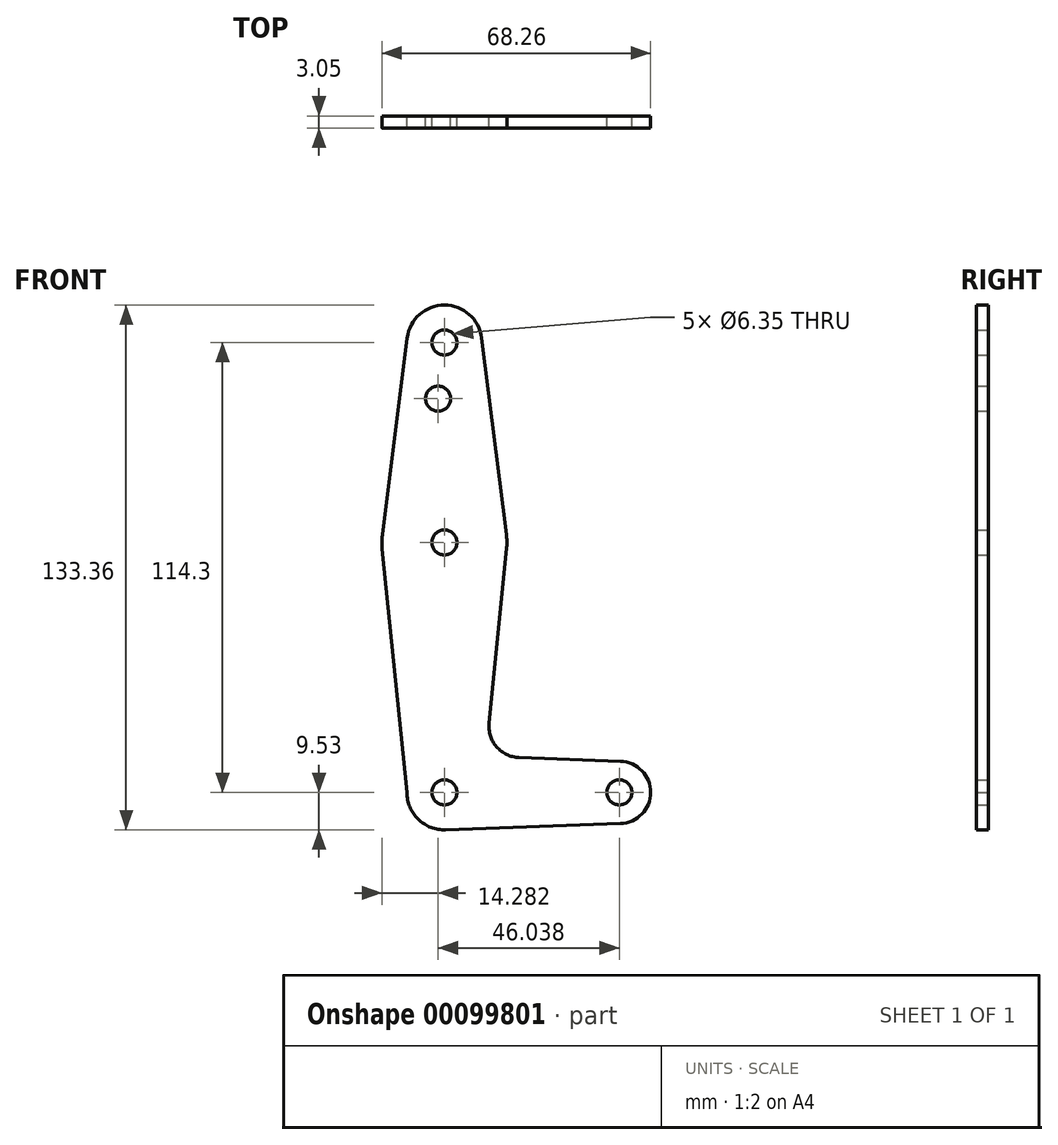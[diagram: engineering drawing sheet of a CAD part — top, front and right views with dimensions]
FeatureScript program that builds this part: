
annotation { "Feature Type Name" : "Feature", "Feature Type Description" : "" }
export const myFeature = defineFeature(function(context is Context, id is Id, definition is map)
    precondition{}
    {
        {
            var Q0;
            Q0=qCreatedBy(makeId("Front.planeOp"),FACE);
            var sketch = newSketch(context, id + "F0", { "sketchPlane" : qUnion([Q0])});
            skLineSegment(sketch, "E0", {"start": v(0, 0) * mm, "end": v(0, 114.3) * mm, "construction": true});
            skCircle(sketch, "E1", {"center": v(0, 114.3) * mm, "radius": 9.53 * mm});
            skLineSegment(sketch, "E2", {"start": v(0, 0) * mm, "end": v(44.45, 0) * mm, "construction": true});
            skCircle(sketch, "E3", {"center": v(44.45, 0) * mm, "radius": 7.94 * mm});
            skCircle(sketch, "E4", {"center": v(0, 0) * mm, "radius": 9.53 * mm});
            skCircle(sketch, "E5", {"center": v(-1.59, 100.03) * mm, "radius": 3.18 * mm});
            skCircle(sketch, "E6", {"center": v(0, 114.3) * mm, "radius": 3.18 * mm});
            skCircle(sketch, "E7", {"center": v(0, 63.5) * mm, "radius": 3.18 * mm});
            skCircle(sketch, "E8", {"center": v(44.45, 0) * mm, "radius": 3.18 * mm});
            skCircle(sketch, "E9", {"center": v(0, 0) * mm, "radius": 3.18 * mm});
            skLineSegment(sketch, "E10", {"start": v(44.73, -7.93) * mm, "end": v(0, -9.53) * mm});
            skLineSegment(sketch, "E11", {"start": v(44.73, 7.93) * mm, "end": v(18.97, 8.85) * mm});
            skCircle(sketch, "E12", {"center": v(0, 63.5) * mm, "radius": 15.88 * mm});
            skLineSegment(sketch, "E13", {"start": v(-9.45, 115.5) * mm, "end": v(-15.75, 65.48) * mm});
            skLineSegment(sketch, "E14", {"start": v(9.45, 115.5) * mm, "end": v(15.75, 65.48) * mm});
            skLineSegment(sketch, "E15", {"start": v(15.8, 61.91) * mm, "end": v(11.34, 17.6) * mm});
            skLineSegment(sketch, "E16", {"start": v(-9.52, 0) * mm, "end": v(-15.8, 61.9) * mm});
            skPoint(sketch, "E17.newPointB", {"position": v(0, 9.53) * mm});
            skArc(sketch, "E17.filletArc", {"start": v(11.34, 17.6) * mm, "mid": v(13.26, 11.57) * mm, "end": v(18.97, 8.85) * mm});
            skSolve(sketch);
        }
        {
            var Q0;
            Q0 = qSketchRegion(id + "F0", true);
            extrude(context, id + "F1", {"entities" : qUnion([Q0]), "depth" : 3.05 * mm});
        }
    });
